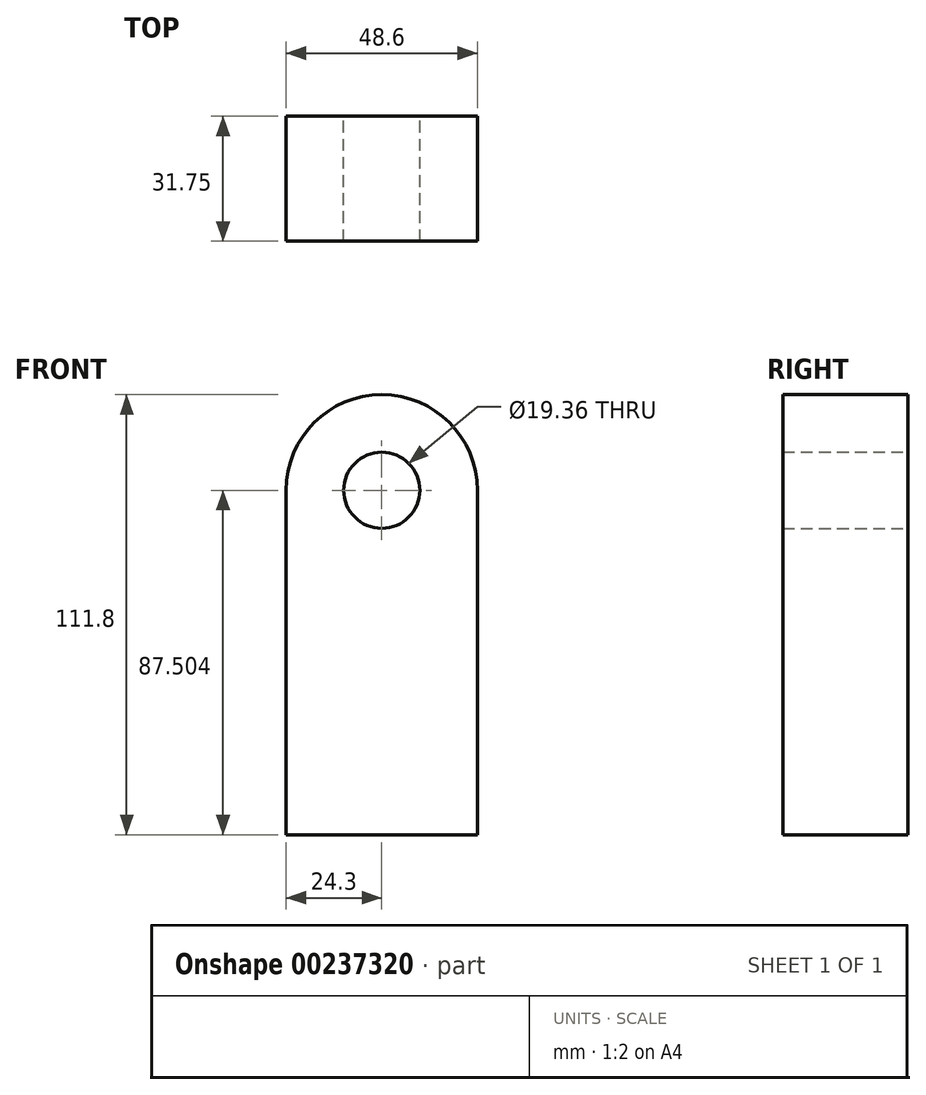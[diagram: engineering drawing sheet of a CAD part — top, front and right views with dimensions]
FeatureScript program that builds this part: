
annotation { "Feature Type Name" : "Feature", "Feature Type Description" : "" }
export const myFeature = defineFeature(function(context is Context, id is Id, definition is map)
    precondition{}
    {
        {
            var Q0;
            Q0=qCreatedBy(makeId("Front.planeOp"),FACE);
            var sketch = newSketch(context, id + "F0", { "sketchPlane" : qUnion([Q0])});
            skLineSegment(sketch, "E0.bottom", {"start": v(24.3, -43.75) * mm, "end": v(-24.3, -43.75) * mm});
            skLineSegment(sketch, "E0.left", {"start": v(24.3, -43.75) * mm, "end": v(24.3, 43.75) * mm});
            skLineSegment(sketch, "E0.right", {"start": v(-24.3, -43.75) * mm, "end": v(-24.3, 43.75) * mm});
            skPoint(sketch, "E0.middle", {"position": v(0, 0) * mm});
            skArc(sketch, "E1", {"start": v(-24.3, 43.75) * mm, "mid": v(0, 68.05) * mm, "end": v(24.3, 43.75) * mm});
            skCircle(sketch, "E2", {"center": v(0, 43.75) * mm, "radius": 9.68 * mm});
            skSolve(sketch);
        }
        {
            var Q0;
            Q0 = qSketchRegion(id + "F0", true);
            extrude(context, id + "F1", {"entities" : qUnion([Q0]), "depth" : 31.75 * mm});
        }
    });
